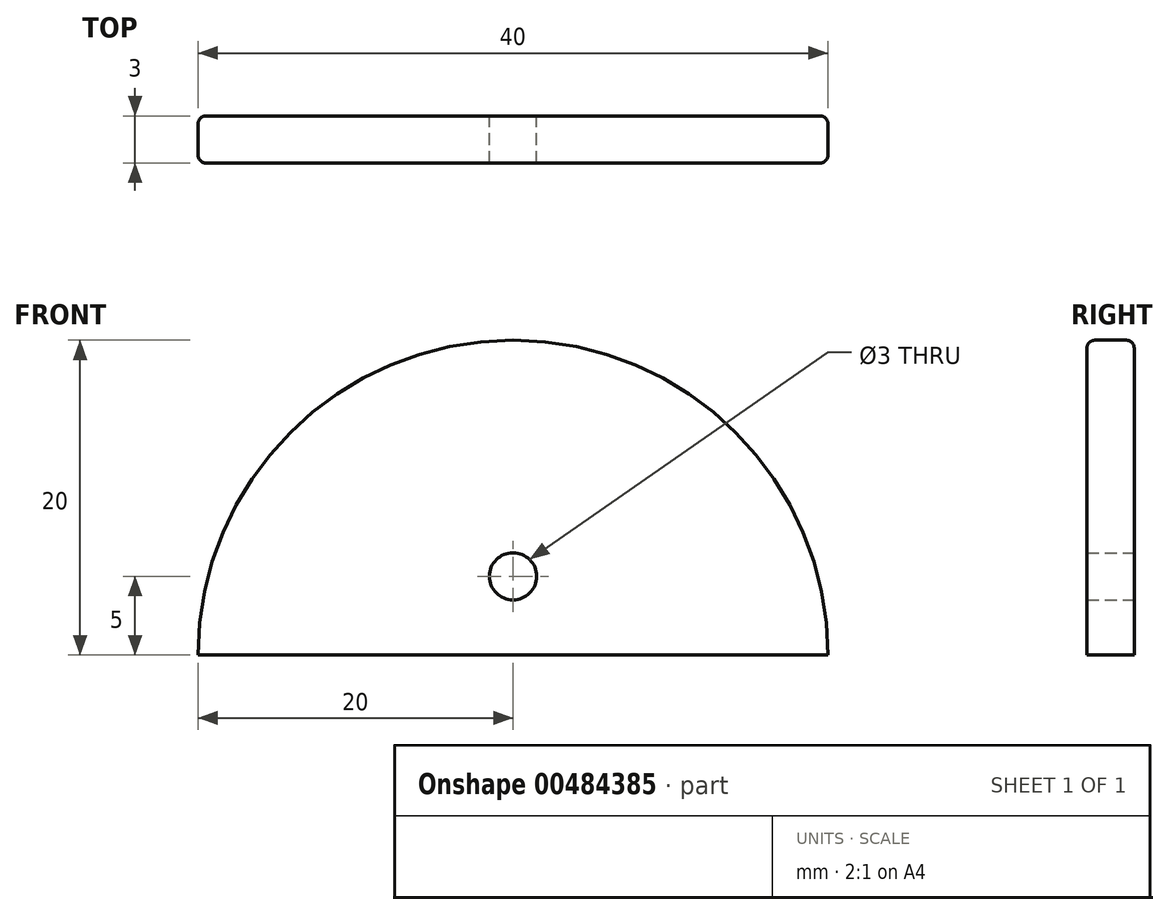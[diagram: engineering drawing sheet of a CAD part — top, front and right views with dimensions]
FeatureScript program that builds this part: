
annotation { "Feature Type Name" : "Feature", "Feature Type Description" : "" }
export const myFeature = defineFeature(function(context is Context, id is Id, definition is map)
    precondition{}
    {
        {
            var Q0;
            Q0=qCreatedBy(makeId("Front.planeOp"),FACE);
            var sketch = newSketch(context, id + "F0", { "sketchPlane" : qUnion([Q0])});
            skArc(sketch, "E0", {"start": v(20, 0) * mm, "mid": v(0, 20) * mm, "end": v(-20, 0) * mm});
            skLineSegment(sketch, "E1", {"start": v(-20, 0) * mm, "end": v(20, 0) * mm});
            skCircle(sketch, "E2", {"center": v(0, 5) * mm, "radius": 1.5 * mm});
            skSolve(sketch);
        }
        {
            var Q0;
            Q0=makeQuery(id+"F0.imprint","IMPRINT",FACE,{"disambiguationData":[TD([[makeQuery(id+"F0.imprint","IMPRINT",EDGE,{"derivedFrom":sQuery(id+"F0.wireOp",EDGE,"E0")}),1.0]])]});
            extrude(context, id + "F1", {"entities" : qUnion([Q0]), "depth" : 1.5 * mm, "offsetDistance" : 25 * mm, "hasSecondDirection" : true, "secondDirectionOppositeDirection" : true, "secondDirectionDepth" : 1.5 * mm});
        }
        {
            var Q0;
            Q0=makeQuery(id+"F1.opExtrude","CAP_EDGE",EDGE,{"disambiguationData":[OSD([sQuery(id+"F0.wireOp",EDGE,"E0")])],"isStart":false});
            var Q1;
            Q1=makeQuery(id+"F1.opExtrude","CAP_EDGE",EDGE,{"disambiguationData":[OSD([sQuery(id+"F0.wireOp",EDGE,"E0")])],"isStart":true});
            fillet(context, id + "F2", {"entities" : qUnion([Q0, Q1]), "radius" : .5 * mm, "tangentPropagation" : true, "allowEdgeOverflow" : false});
        }
    });
